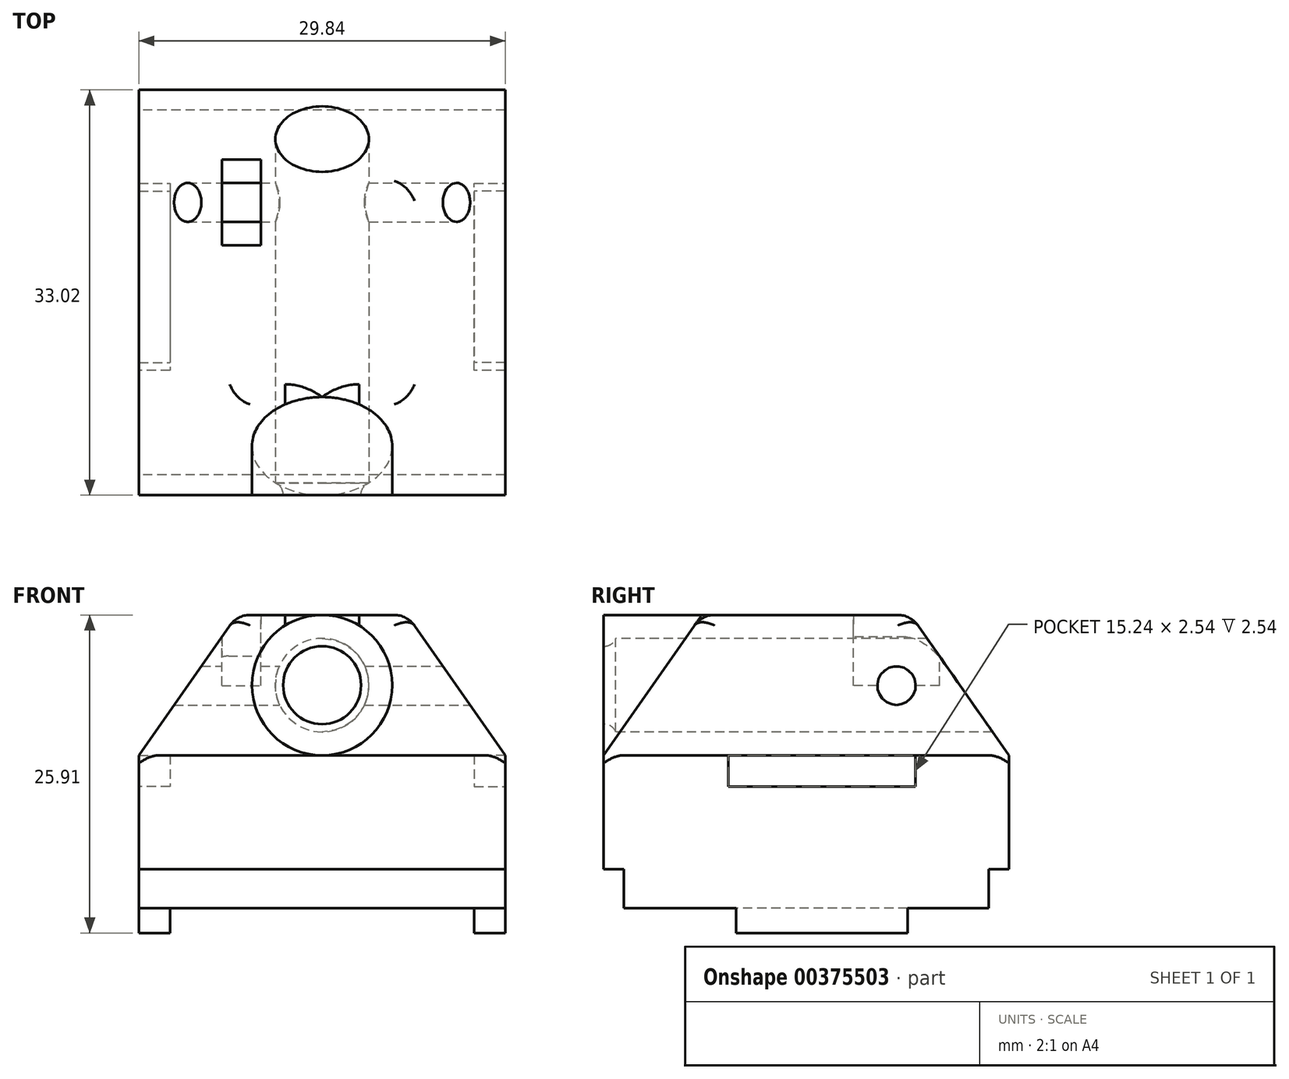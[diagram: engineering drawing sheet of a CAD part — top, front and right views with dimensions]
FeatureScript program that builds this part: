
annotation { "Feature Type Name" : "Feature", "Feature Type Description" : "" }
export const myFeature = defineFeature(function(context is Context, id is Id, definition is map)
    precondition{}
    {
        {
            var Q0;
            Q0=qCreatedBy(makeId("Top.planeOp"),FACE);
            var sketch = newSketch(context, id + "F0", { "sketchPlane" : qUnion([Q0])});
            skLineSegment(sketch, "E0.bottom", {"start": v(-14.92, 16.5) * mm, "end": v(14.92, 16.5) * mm});
            skLineSegment(sketch, "E0.top", {"start": v(-14.92, -16.51) * mm, "end": v(14.92, -16.51) * mm});
            skLineSegment(sketch, "E0.left", {"start": v(-14.92, 16.5) * mm, "end": v(-14.92, -16.51) * mm});
            skLineSegment(sketch, "E0.right", {"start": v(14.92, 16.5) * mm, "end": v(14.92, -16.51) * mm});
            skPoint(sketch, "E0.middle", {"position": v(0, 0) * mm});
            skSolve(sketch);
        }
        {
            var Q0;
            Q0 = qSketchRegion(id + "F0", true);
            extrude(context, id + "F1", {"entities" : qUnion([Q0]), "depth" : 9.9 * mm});
        }
        {
            var Q0;
            Q0=makeQuery(id+"F1.opExtrude","SWEPT_FACE",FACE,{"disambiguationData":[OSD([sQuery(id+"F0.wireOp",EDGE,"E0.left")])]});
            var sketch = newSketch(context, id + "F2", { "sketchPlane" : qUnion([Q0])});
            skLineSegment(sketch, "E1.bottom", {"start": v(-16.5, 0) * mm, "end": v(-14.86, 0) * mm});
            skLineSegment(sketch, "E1.top", {"start": v(-16.5, 3.17) * mm, "end": v(-14.86, 3.17) * mm});
            skLineSegment(sketch, "E1.left", {"start": v(-16.5, 0) * mm, "end": v(-16.5, 3.17) * mm});
            skLineSegment(sketch, "E1.right", {"start": v(-14.86, 0) * mm, "end": v(-14.86, 3.17) * mm});
            skLineSegment(sketch, "E2.bottom", {"start": v(16.51, 0) * mm, "end": v(14.86, 0) * mm});
            skLineSegment(sketch, "E2.top", {"start": v(16.51, 3.18) * mm, "end": v(14.86, 3.18) * mm});
            skLineSegment(sketch, "E2.left", {"start": v(16.51, 0) * mm, "end": v(16.51, 3.18) * mm});
            skLineSegment(sketch, "E2.right", {"start": v(14.86, 0) * mm, "end": v(14.86, 3.18) * mm});
            skSolve(sketch);
        }
        {
            var Q0;
            Q0 = qSketchRegion(id + "F2", true);
            extrude(context, id + "F3", {"entities" : qUnion([Q0]), "operationType" : NewBodyOperationType.REMOVE, "endBound" : BoundingType.THROUGH_ALL, "oppositeDirection" : true, "depth" : 25 * mm});
        }
        {
            var Q0;
            Q0=makeQuery(id+"F1.opExtrude","CAP_FACE",FACE,{"disambiguationData":[OSD([sQuery(id+"F0.wireOp",EDGE,"E0.bottom"),sQuery(id+"F0.wireOp",EDGE,"E0.top"),sQuery(id+"F0.wireOp",EDGE,"E0.left"),sQuery(id+"F0.wireOp",EDGE,"E0.right")])],"isStart":false});
            var sketch = newSketch(context, id + "F4", { "sketchPlane" : qUnion([Q0])});
            skLineSegment(sketch, "E3", {"start": v(14.92, -16.51) * mm, "end": v(14.92, -6.35) * mm});
            skLineSegment(sketch, "E4", {"start": v(14.92, -6.35) * mm, "end": v(12.38, -6.35) * mm});
            skLineSegment(sketch, "E5", {"start": v(12.38, -6.35) * mm, "end": v(12.38, 8.89) * mm});
            skLineSegment(sketch, "E6", {"start": v(12.38, 8.89) * mm, "end": v(14.92, 8.89) * mm});
            skLineSegment(sketch, "E7", {"start": v(14.92, 8.89) * mm, "end": v(14.92, 16.5) * mm});
            skLineSegment(sketch, "E8", {"start": v(14.92, 16.5) * mm, "end": v(-14.92, 16.5) * mm});
            skLineSegment(sketch, "E9", {"start": v(-14.92, 16.5) * mm, "end": v(-14.92, 8.89) * mm});
            skLineSegment(sketch, "E10", {"start": v(-14.92, 8.89) * mm, "end": v(-12.38, 8.89) * mm});
            skLineSegment(sketch, "E11", {"start": v(-12.38, 8.89) * mm, "end": v(-12.38, -6.35) * mm});
            skLineSegment(sketch, "E12", {"start": v(-12.38, -6.35) * mm, "end": v(-14.92, -6.35) * mm});
            skLineSegment(sketch, "E13", {"start": v(-14.92, -6.35) * mm, "end": v(-14.92, -16.51) * mm});
            skLineSegment(sketch, "E14", {"start": v(-14.92, -16.51) * mm, "end": v(14.92, -16.51) * mm});
            skLineSegment(sketch, "E15", {"start": v(12.38, 1.27) * mm, "end": v(-12.38, 1.27) * mm, "construction": true});
            skSolve(sketch);
        }
        {
            var Q0;
            Q0 = qSketchRegion(id + "F4", true);
            extrude(context, id + "F5", {"entities" : qUnion([Q0]), "operationType" : NewBodyOperationType.ADD, "depth" : 2.54 * mm});
        }
        {
            var Q0;
            Q0=makeQuery(id+"F5.opExtrude","CAP_FACE",FACE,{"disambiguationData":[OSD([sQuery(id+"F4.wireOp",EDGE,"E3"),sQuery(id+"F4.wireOp",EDGE,"E4"),sQuery(id+"F4.wireOp",EDGE,"E5"),sQuery(id+"F4.wireOp",EDGE,"E6"),sQuery(id+"F4.wireOp",EDGE,"E7"),sQuery(id+"F4.wireOp",EDGE,"E8"),sQuery(id+"F4.wireOp",EDGE,"E9"),sQuery(id+"F4.wireOp",EDGE,"E10"),sQuery(id+"F4.wireOp",EDGE,"E11"),sQuery(id+"F4.wireOp",EDGE,"E12"),sQuery(id+"F4.wireOp",EDGE,"E13"),sQuery(id+"F4.wireOp",EDGE,"E14")])],"isStart":false});
            var sketch = newSketch(context, id + "F6", { "sketchPlane" : qUnion([Q0])});
            skLineSegment(sketch, "E16.bottom", {"start": v(14.92, -16.51) * mm, "end": v(-14.92, -16.51) * mm});
            skLineSegment(sketch, "E16.top", {"start": v(14.92, 16.51) * mm, "end": v(-14.92, 16.5) * mm});
            skLineSegment(sketch, "E16.left", {"start": v(14.92, -16.51) * mm, "end": v(14.92, 16.51) * mm});
            skLineSegment(sketch, "E16.right", {"start": v(-14.92, -16.51) * mm, "end": v(-14.92, 16.5) * mm});
            skSolve(sketch);
        }
        {
            var Q0;
            Q0 = qSketchRegion(id + "F6", true);
            extrude(context, id + "F7", {"entities" : qUnion([Q0]), "operationType" : NewBodyOperationType.ADD, "depth" : 11.43 * mm, "hasDraft" : true, "draftAngle" : 35 * degree, "draftPullDirection" : true});
        }
        {
            var Q0;
            Q0=qCreatedBy(makeId("Front.planeOp"),FACE);
            var sketch = newSketch(context, id + "F8", { "sketchPlane" : qUnion([Q0])});
            skCircle(sketch, "E17", {"center": v(0, 18.16) * mm, "radius": 3.81 * mm});
            skLineSegment(sketch, "E18", {"start": v(0, 23.88) * mm, "end": v(0, 12.45) * mm, "construction": true});
            skSolve(sketch);
        }
        {
            var Q0;
            Q0 = qSketchRegion(id + "F8", true);
            extrude(context, id + "F9", {"entities" : qUnion([Q0]), "operationType" : NewBodyOperationType.REMOVE, "endBound" : BoundingType.THROUGH_ALL, "oppositeDirection" : true, "depth" : 25 * mm, "hasSecondDirection" : true, "secondDirectionBound" : SecondDirectionBoundingType.THROUGH_ALL, "secondDirectionOppositeDirection" : false, "secondDirectionDepth" : 25 * mm});
        }
        {
            var Q0;
            Q0=makeQuery(id+"F5.boolean.opBoolean","MERGE",FACE,{"derivedFrom":[makeQuery(id+"F1.opExtrude","SWEPT_FACE",FACE,{"disambiguationData":[OSD([sQuery(id+"F0.wireOp",EDGE,"E0.top")])]}),makeQuery(id+"F5.opExtrude","SWEPT_FACE",FACE,{"disambiguationData":[OSD([sQuery(id+"F4.wireOp",EDGE,"E14")])]})]});
            var sketch = newSketch(context, id + "F10", { "sketchPlane" : qUnion([Q0])});
            skCircle(sketch, "E19", {"center": v(0, 18.16) * mm, "radius": 3.81 * mm});
            skCircle(sketch, "E20", {"center": v(0, 18.16) * mm, "radius": 5.71 * mm});
            skPoint(sketch, "E21", {"position": v(0, 23.88) * mm});
            skSolve(sketch);
        }
        {
            var Q0;
            Q0 = qSketchRegion(id + "F10", true);
            var Q1;
            Q1=makeQuery(id+"F7.opExtrude","SWEPT_FACE",FACE,{"disambiguationData":[OSD([sQuery(id+"F6.wireOp",EDGE,"E16.bottom")])]});
            extrude(context, id + "F11", {"entities" : qUnion([Q0]), "operationType" : NewBodyOperationType.ADD, "endBound" : BoundingType.UP_TO_SURFACE, "oppositeDirection" : true, "endBoundEntityFace" : qUnion([Q1]), "depth" : 25 * mm});
        }
        {
            var Q0;
            Q0=makeQuery(id+"F11.opExtrude","CAP_FACE",FACE,{"disambiguationData":[OSD([sQuery(id+"F10.wireOp",EDGE,"E19"),sQuery(id+"F10.wireOp",EDGE,"E20")])],"isStart":true});
            var sketch = newSketch(context, id + "F12", { "sketchPlane" : qUnion([Q0])});
            skCircle(sketch, "E22", {"center": v(0, 18.16) * mm, "radius": 5.71 * mm});
            skCircle(sketch, "E23", {"center": v(0, 18.16) * mm, "radius": 3.18 * mm});
            skSolve(sketch);
        }
        {
            var Q0;
            Q0 = qSketchRegion(id + "F12", true);
            extrude(context, id + "F13", {"entities" : qUnion([Q0]), "operationType" : NewBodyOperationType.ADD, "oppositeDirection" : true, "depth" : 1 * mm});
        }
        {
            var Q0;
            Q0=makeQuery(id+"F7.opExtrude","CAP_FACE",FACE,{"disambiguationData":[OSD([sQuery(id+"F6.wireOp",EDGE,"E16.bottom"),sQuery(id+"F6.wireOp",EDGE,"E16.top"),sQuery(id+"F6.wireOp",EDGE,"E16.left"),sQuery(id+"F6.wireOp",EDGE,"E16.right")])],"isStart":false});
            var Q1;
            Q1=makeQuery(id+"F7.opExtrude","SWEPT_EDGE",EDGE,{"disambiguationData":[OSD([sQuery(id+"F6.wireOp",EDGE,"E16.top"),sQuery(id+"F6.wireOp",EDGE,"E16.left")])]});
            var Q2;
            Q2=makeQuery(id+"F7.opExtrude","SWEPT_EDGE",EDGE,{"disambiguationData":[OSD([sQuery(id+"F6.wireOp",EDGE,"E16.bottom"),sQuery(id+"F6.wireOp",EDGE,"E16.left")])]});
            var Q3;
            Q3=makeQuery(id+"F7.opExtrude","SWEPT_EDGE",EDGE,{"disambiguationData":[OSD([sQuery(id+"F6.wireOp",EDGE,"E16.top"),sQuery(id+"F6.wireOp",EDGE,"E16.right")])]});
            var Q4;
            Q4=makeQuery(id+"F7.opExtrude","SWEPT_EDGE",EDGE,{"disambiguationData":[OSD([sQuery(id+"F6.wireOp",EDGE,"E16.bottom"),sQuery(id+"F6.wireOp",EDGE,"E16.right")])]});
            fillet(context, id + "F14", {"entities" : qUnion([Q0, Q1, Q2, Q3, Q4]), "radius" : 2 * mm, "tangentPropagation" : true, "allowEdgeOverflow" : false});
        }
        {
            var Q0;
            Q0=makeQuery(id+"F7.opExtrude","CAP_FACE",FACE,{"disambiguationData":[OSD([sQuery(id+"F6.wireOp",EDGE,"E16.bottom"),sQuery(id+"F6.wireOp",EDGE,"E16.top"),sQuery(id+"F6.wireOp",EDGE,"E16.left"),sQuery(id+"F6.wireOp",EDGE,"E16.right")])],"isStart":false});
            var sketch = newSketch(context, id + "F15", { "sketchPlane" : qUnion([Q0])});
            skLineSegment(sketch, "E24.bottom", {"start": v(-8.18, 10.85) * mm, "end": v(-5, 10.85) * mm});
            skLineSegment(sketch, "E24.top", {"start": v(-8.18, 3.85) * mm, "end": v(-5, 3.85) * mm});
            skLineSegment(sketch, "E24.left", {"start": v(-8.18, 10.85) * mm, "end": v(-8.18, 3.85) * mm});
            skLineSegment(sketch, "E24.right", {"start": v(-5, 10.85) * mm, "end": v(-5, 3.85) * mm});
            skLineSegment(sketch, "E25", {"start": v(0, -16.51) * mm, "end": v(0, 16.5) * mm, "construction": true});
            skPoint(sketch, "E25.endSnap0", {"position": v(0, 7.47) * mm});
            skPoint(sketch, "E26", {"position": v(-5, 7.35) * mm});
            skPoint(sketch, "E27", {"position": v(0, -15.51) * mm});
            skSolve(sketch);
        }
        {
            var Q0;
            Q0 = qSketchRegion(id + "F15", true);
            extrude(context, id + "F16", {"entities" : qUnion([Q0]), "operationType" : NewBodyOperationType.REMOVE, "oppositeDirection" : true, "depth" : 5.75 * mm + .275 / 50.8 * mm});
        }
        {
            var Q0;
            Q0=qCreatedBy(makeId("Right.planeOp"),FACE);
            var sketch = newSketch(context, id + "F17", { "sketchPlane" : qUnion([Q0])});
            skLineSegment(sketch, "E28", {"start": v(-16.51, 18.13) * mm, "end": v(21, 18.13) * mm, "construction": true});
            skLineSegment(sketch, "E29", {"start": v(-16.51, 21.26) * mm, "end": v(-16.51, 14.99) * mm, "construction": true});
            skCircle(sketch, "E30", {"center": v(7.35, 18.13) * mm, "radius": 1.59 * mm});
            skPoint(sketch, "E31", {"position": v(-15.51, 18.13) * mm});
            skSolve(sketch);
        }
        {
            var Q0;
            Q0 = qSketchRegion(id + "F17", true);
            extrude(context, id + "F18", {"entities" : qUnion([Q0]), "operationType" : NewBodyOperationType.REMOVE, "oppositeDirection" : true, "depth" : 25 * mm, "hasSecondDirection" : true, "secondDirectionBound" : SecondDirectionBoundingType.THROUGH_ALL, "secondDirectionOppositeDirection" : false, "secondDirectionDepth" : 25 * mm});
        }
        {
            var Q0;
            Q0=makeQuery(id+"F13.opExtrude","CAP_EDGE",EDGE,{"disambiguationData":[OSD([sQuery(id+"F12.wireOp",EDGE,"E23")])],"isStart":false});
            fillet(context, id + "F19", {"entities" : qUnion([Q0]), "radius" : 1 * mm, "tangentPropagation" : true, "allowEdgeOverflow" : false});
        }
        {
            var Q0;
            Q0=makeQuery(id+"F1.opExtrude","CAP_FACE",FACE,{"disambiguationData":[OSD([sQuery(id+"F0.wireOp",EDGE,"E0.bottom"),sQuery(id+"F0.wireOp",EDGE,"E0.top"),sQuery(id+"F0.wireOp",EDGE,"E0.left"),sQuery(id+"F0.wireOp",EDGE,"E0.right")])],"isStart":true});
            var sketch = newSketch(context, id + "F20", { "sketchPlane" : qUnion([Q0])});
            skLineSegment(sketch, "E32.bottom", {"start": v(-14.92, -8.25) * mm, "end": v(-12.38, -8.25) * mm});
            skLineSegment(sketch, "E32.top", {"start": v(-14.92, 5.72) * mm, "end": v(-12.38, 5.72) * mm});
            skLineSegment(sketch, "E32.left", {"start": v(-14.92, -8.25) * mm, "end": v(-14.92, 5.72) * mm});
            skLineSegment(sketch, "E32.right", {"start": v(-12.38, -8.25) * mm, "end": v(-12.38, 5.72) * mm});
            skLineSegment(sketch, "E33.bottom", {"start": v(14.92, -8.25) * mm, "end": v(12.38, -8.25) * mm});
            skLineSegment(sketch, "E33.top", {"start": v(14.92, 5.72) * mm, "end": v(12.38, 5.72) * mm});
            skLineSegment(sketch, "E33.left", {"start": v(14.92, -8.25) * mm, "end": v(14.92, 5.72) * mm});
            skLineSegment(sketch, "E33.right", {"start": v(12.38, -8.25) * mm, "end": v(12.38, 5.72) * mm});
            skPoint(sketch, "E34", {"position": v(-12.38, -1.27) * mm});
            skPoint(sketch, "E35", {"position": v(12.38, -1.27) * mm});
            skLineSegment(sketch, "E36", {"start": v(-12.38, -1.27) * mm, "end": v(12.38, -1.27) * mm, "construction": true});
            skSolve(sketch);
        }
        {
            var Q0;
            Q0 = qSketchRegion(id + "F20", true);
            extrude(context, id + "F21", {"entities" : qUnion([Q0]), "operationType" : NewBodyOperationType.ADD, "depth" : 2.03 * mm});
        }
    });
